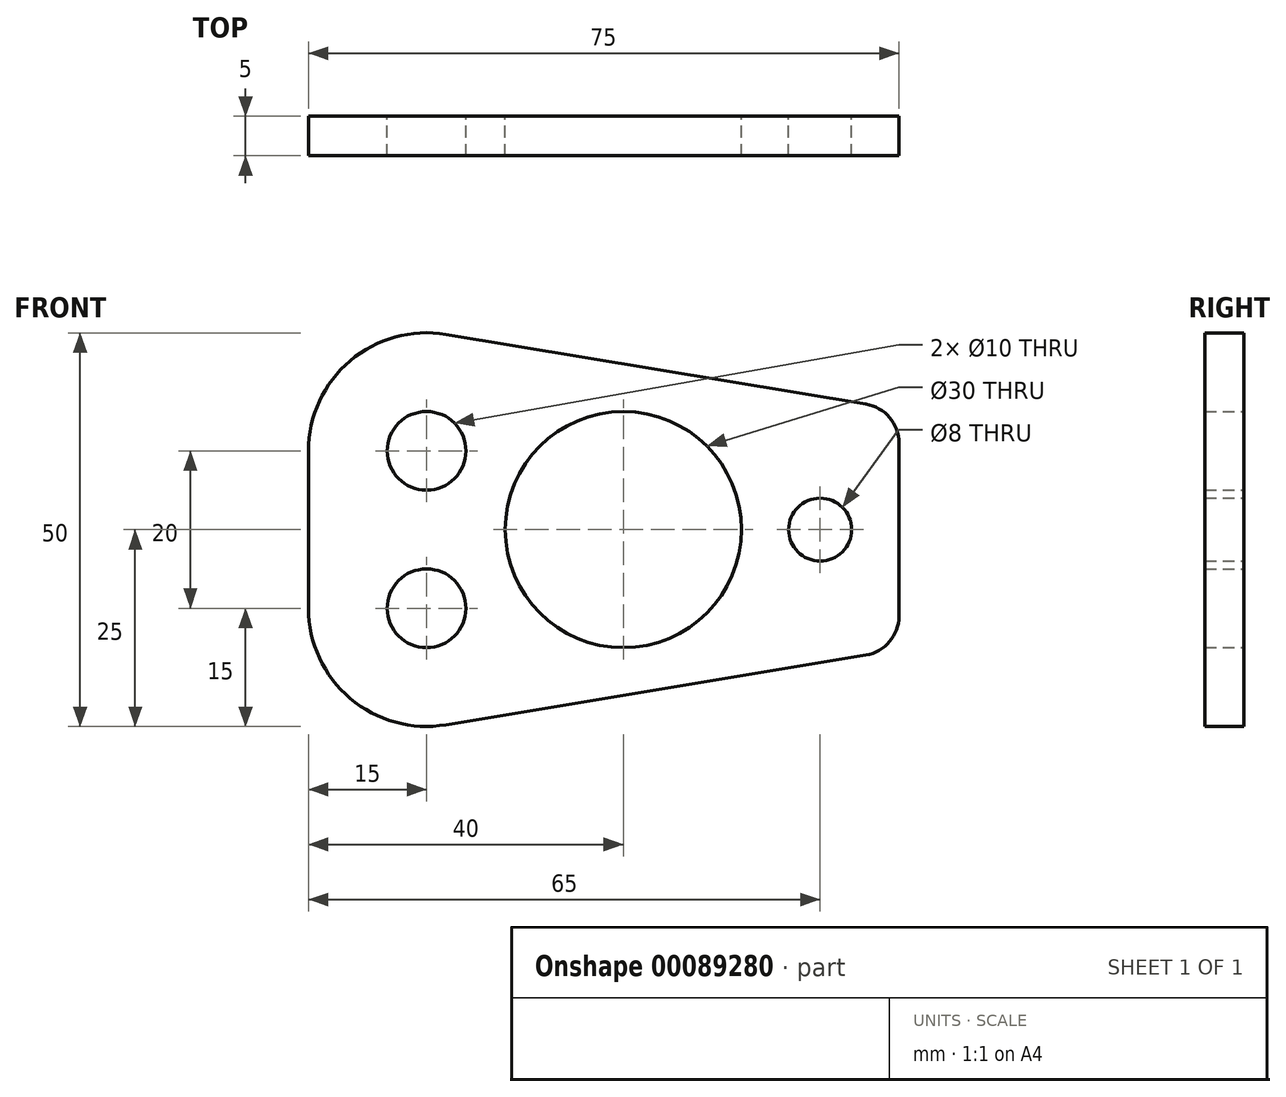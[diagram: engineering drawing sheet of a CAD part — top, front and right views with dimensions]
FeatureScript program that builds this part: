
annotation { "Feature Type Name" : "Feature", "Feature Type Description" : "" }
export const myFeature = defineFeature(function(context is Context, id is Id, definition is map)
    precondition{}
    {
        {
            var Q0;
            Q0=qCreatedBy(makeId("Front.planeOp"),FACE);
            var sketch = newSketch(context, id + "F0", { "sketchPlane" : qUnion([Q0])});
            skCircle(sketch, "E0", {"center": v(0, 0) * mm, "radius": 15 * mm});
            skCircle(sketch, "E1", {"center": v(-25, 10) * mm, "radius": 5 * mm});
            skCircle(sketch, "E2", {"center": v(-25, -10) * mm, "radius": 5 * mm});
            skCircle(sketch, "E3", {"center": v(25, 0) * mm, "radius": 4 * mm});
            skArc(sketch, "E4", {"start": v(-22.54, 24.8) * mm, "mid": v(-34.7, 21.44) * mm, "end": v(-40, 10) * mm});
            skArc(sketch, "E5", {"start": v(-40, -10) * mm, "mid": v(-34.7, -21.44) * mm, "end": v(-22.54, -24.8) * mm});
            skLineSegment(sketch, "E6", {"start": v(-40, 10) * mm, "end": v(-40, -10) * mm});
            skArc(sketch, "E7", {"start": v(35, 11) * mm, "mid": v(33.81, 14.23) * mm, "end": v(30.82, 15.93) * mm});
            skArc(sketch, "E8", {"start": v(30.82, -15.93) * mm, "mid": v(33.81, -14.23) * mm, "end": v(35, -11) * mm});
            skLineSegment(sketch, "E9", {"start": v(-22.54, -24.8) * mm, "end": v(30.82, -15.93) * mm});
            skLineSegment(sketch, "E10", {"start": v(-22.54, 24.8) * mm, "end": v(30.82, 15.93) * mm});
            skLineSegment(sketch, "E11", {"start": v(35, 11) * mm, "end": v(35, -11) * mm});
            skPoint(sketch, "E12.orphan", {"position": v(-40, 0) * mm});
            skPoint(sketch, "E13.end.orphan", {"position": v(35, 0) * mm});
            skSolve(sketch);
        }
        {
            var Q0;
            Q0=makeQuery(id+"F0.imprint","IMPRINT",FACE,{"disambiguationData":[TD([[makeQuery(id+"F0.imprint","IMPRINT",EDGE,{"derivedFrom":sQuery(id+"F0.wireOp",EDGE,"E0")}),-1.0]])]});
            extrude(context, id + "F1", {"entities" : qUnion([Q0]), "depth" : 5 * mm});
        }
    });
